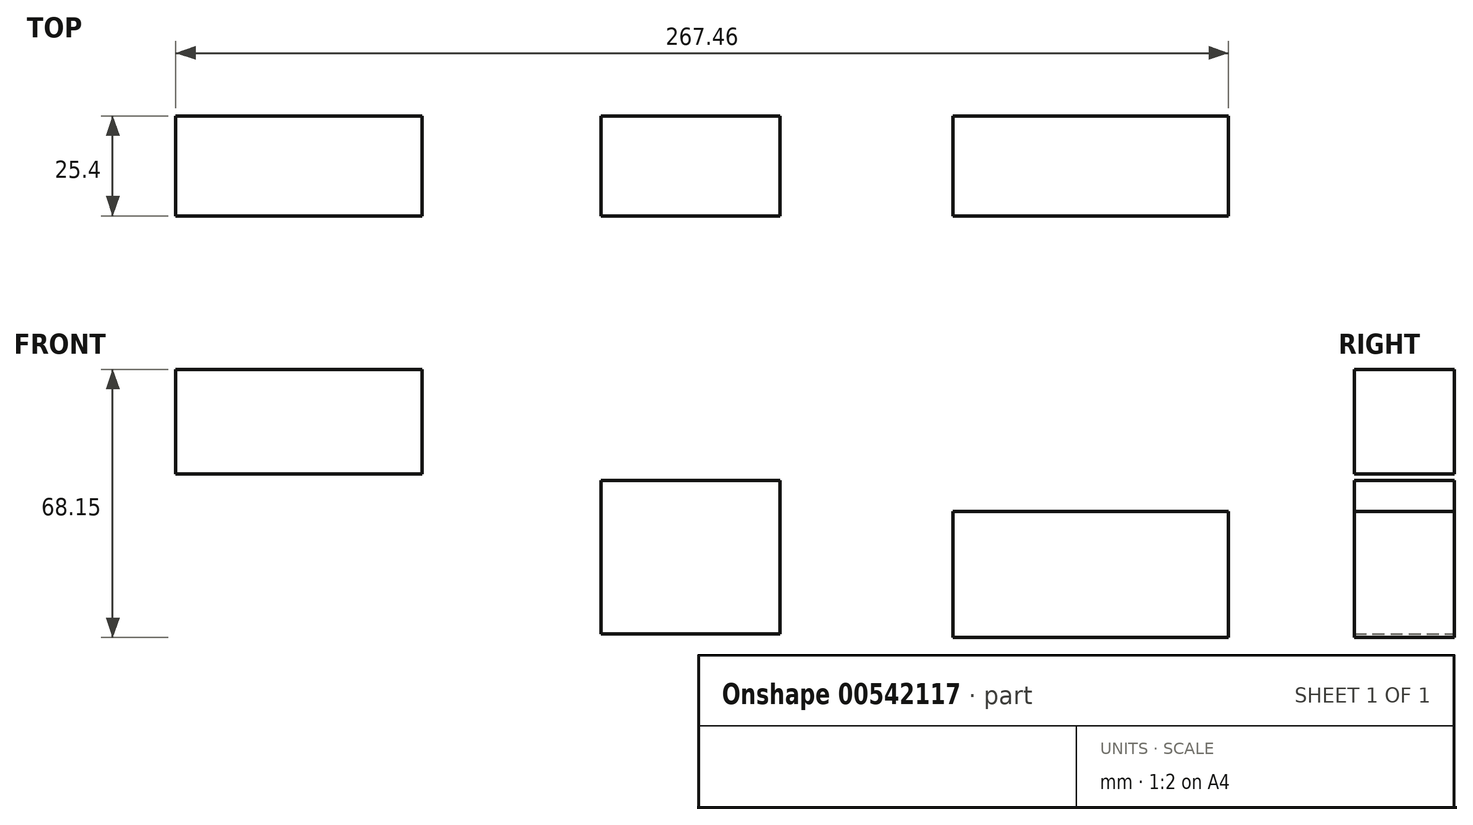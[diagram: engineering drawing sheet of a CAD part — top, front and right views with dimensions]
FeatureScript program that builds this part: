
annotation { "Feature Type Name" : "Feature", "Feature Type Description" : "" }
export const myFeature = defineFeature(function(context is Context, id is Id, definition is map)
    precondition{}
    {
        {
            var Q0;
            Q0=qCreatedBy(makeId("Front.planeOp"),FACE);
            var sketch = newSketch(context, id + "F0", { "sketchPlane" : qUnion([Q0])});
            skLineSegment(sketch, "E0.bottom", {"start": v(-135.05, 47.57) * mm, "end": v(-72.41, 47.57) * mm});
            skLineSegment(sketch, "E0.top", {"start": v(-135.05, 20.99) * mm, "end": v(-72.41, 20.99) * mm});
            skLineSegment(sketch, "E0.left", {"start": v(-135.05, 47.57) * mm, "end": v(-135.05, 20.99) * mm});
            skLineSegment(sketch, "E0.right", {"start": v(-72.41, 47.57) * mm, "end": v(-72.41, 20.99) * mm});
            skLineSegment(sketch, "E1.bottom", {"start": v(-26.96, 19.3) * mm, "end": v(18.5, 19.3) * mm});
            skLineSegment(sketch, "E1.top", {"start": v(-26.96, -19.63) * mm, "end": v(18.5, -19.63) * mm});
            skLineSegment(sketch, "E1.left", {"start": v(-26.96, 19.3) * mm, "end": v(-26.96, -19.63) * mm});
            skLineSegment(sketch, "E1.right", {"start": v(18.5, 19.3) * mm, "end": v(18.5, -19.63) * mm});
            skLineSegment(sketch, "E2.bottom", {"start": v(62.37, 11.53) * mm, "end": v(132.4, 11.53) * mm});
            skLineSegment(sketch, "E2.top", {"start": v(62.37, -20.58) * mm, "end": v(132.4, -20.58) * mm});
            skLineSegment(sketch, "E2.left", {"start": v(62.37, 11.53) * mm, "end": v(62.37, -20.58) * mm});
            skLineSegment(sketch, "E2.right", {"start": v(132.4, 11.53) * mm, "end": v(132.4, -20.58) * mm});
            skSolve(sketch);
        }
        {
            var Q0;
            Q0 = qSketchRegion(id + "F0", true);
            extrude(context, id + "F1", {"entities" : qUnion([Q0]), "depth" : 25.4 * mm, "offsetDistance" : 25.4 * mm});
        }
    });
